# Revit family: Hager-WITTY ONE WALL MOUNTED-en-SE
name_source: partatom
category: Electrical Fixtures
units: mm (PartAtom-declared; Revit-internal decimal feet)

## family parameters
Always vertical = Yes
Cut with Voids When Loaded = No
Host = Wall
Maintain Annotation Orientation = No
OmniClass Number = 23.75.00.00
OmniClass Title = Climate Control (HVAC)
Part Type = Normal
Room Calculation Point = No
Round Connector Dimension = Use Diameter
Shared = No

## types (2) — shared parameters
BC_METADATA = {"ObjectGuid":"b7395028-ef9e-46b8-b49f-e0fe9c8fa070","ModelGuid":"b1efb829-c177-4a88-8b0d-f632edc25d22","VariantGuid":"c7b0c534-fef0-4725-a2d6-e8a658ebdb92","Revision":"#2","VariantName":"REF 1"}
BC_MODEL_ID = 1528857
BC_OBJECT_ID = 511133
BC_OBJECT_VERSION = #1
Code hager = ADD_EC002883_ECVS_WO
EF000003 - Mounting method = Wall mounting
EF000008 - Width = 250 mm  [stored 0.82021 ft]
EF000040 - Height = 370 mm  [stored 1.21391 ft]
EF000049 - Depth = 150 mm  [stored 0.492126 ft]
EF000458 - With display = No
EF001596 - Housing material = Plastic
EF002136 - Nominal connection power = 11000 W
EF003840 - Input voltage = 400 V
EF004293 - Impact strength = IK08
EF005455 - Frequency = 50/60 Hz
EF005474 - Degree of protection (IP) = IP54
EF007001 - Output voltage DC = 0 V
EF007353 - Max. output current DC = 0 A
EF009078 - Number of charging units = 1
EF009089 - With house connection box = No
EF009300 - Max. power per charging point = 11000 W
EF009305 - Number of socket outlets Type 2 = 1
EF009313 - With energy meter = No
EF009314 - With miniature circuit breaker (MCB) = No
EF009547 - Long-Term Evolution (LTE) = No
EF011072 - IFTTT support available = No
EF012191 - With built-in RFID card reader = Yes
EF012361 - NFC (Near Field Communication) = No
EF013154 - Networkable via Wi-Fi = No
EF014925 - Compatible with Apple HomeKit = No
EF014926 - Compatible with Google Assistant = No
EF014927 - Compatible with Amazon Alexa = No
EF016385 - Mobile communications standard 5G = No
EF017508 - Network-enabled as a master = No
EF017509 - DC residual current detection = Yes
EF017511 - With key switch = No
EF017512 - Export of charging logs = Yes
EF017513 - OpenChargePointProtocoll (OCPP) version = 1.6
EF017515 - Plug and charge (ISO 15118) = No
EF017517 - Network-enabled as an extender = No
EF017663 - Charging cable permanently lockable at charging device = Yes
EF017664 - Networkable via LAN = No
EF017665 - With MID compliant energy meter = No
EF017668 - Static load management integrated = No
EF017669 - Suitable for dynamic load management = Yes
EF017672 - Backend included = No
EF017972 - Operation and configuration by app = Yes
EF025053 - Installation side connection model = 3-phase
EFDE0066 - Calibration law compliant = No
ETIM class code = EC002883
ETIM class name = Charging device E-Mobility
HG000003-Range = WITTY ONE
HG000065-With socket TE = No
HG000099-Onfly Template ID = WittyOne_EVCS_Wall_Mounted
Manufacturer = hager France
Name = WITTY ONE WALL MOUNTED-SE
Name BIM&CO = Electricity
Name hager = ADD_ChargingStation_EC002883
Reference description = ECVS Witty 1x11kW 3P T2S
zero-valued in all types: Default Elevation, EF006577 - Number of CEE socket outlets (IEC 60309), EF008200 - Connectable conductor cross section, EF009091 - Number of earth leakage circuit breakers type A, EF009092 - Number of earth leakage circuit breakers type B, EF009301 - Number of vehicle connectors Type 1, EF009302 - Number of vehicle connectors Type 1 CCS, EF009303 - Number of vehicle connectors Type 2, EF009304 - Number of vehicle connectors Type 2 CCS, EF009306 - Number of vehicle connectors GB AC, EF009307 - Number of vehicle connectors GB DC, EF009308 - Number of socket outlets GB, EF009309 - Number of socket outlets Type 3, EF009310 - Number of vehicle connectors CHAdeMO, EF009311 - Number of household socket outlets

## per-type parameters (varying)
| type | BC_VARIANT_ID | EF014895 - Length of charging cable | HG000004-Manufacturer reference |
| WITTY ONE-1x11kW-3P-XVR111S-WALL MOUNTED | 1164612 | 0 mm  [stored 0 ft] | XVR111S |
| WITTY ONE-1x11kW-3P-XVR111C-WALL MOUNTED | 1164613 | 6500 mm  [stored 21.3255 ft] | XVR111C |

note: column(s) folded — value = type name in every type: Reference

note: [stored X ft] marks values corroborated as IEEE doubles in the binary element streams (Revit-internal decimal feet)
